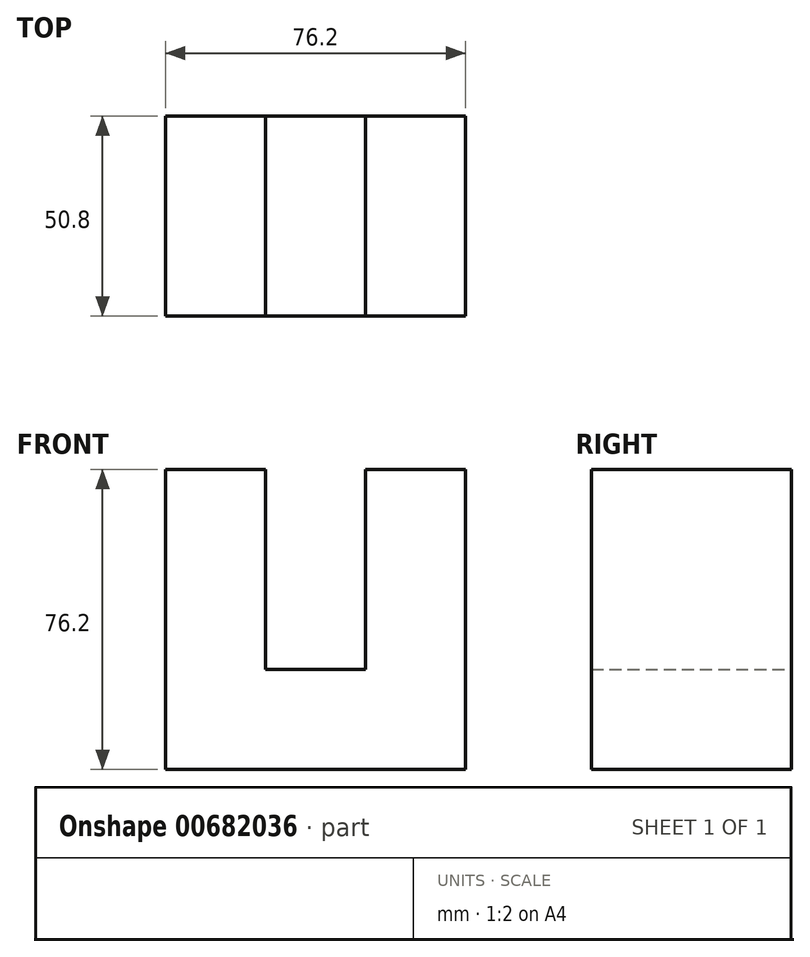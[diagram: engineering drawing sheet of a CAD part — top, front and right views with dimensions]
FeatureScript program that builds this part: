
annotation { "Feature Type Name" : "Feature", "Feature Type Description" : "" }
export const myFeature = defineFeature(function(context is Context, id is Id, definition is map)
    precondition{}
    {
        {
            var Q0;
            Q0=qCreatedBy(makeId("Front.planeOp"),FACE);
            var sketch = newSketch(context, id + "F0", { "sketchPlane" : qUnion([Q0])});
            skLineSegment(sketch, "E0", {"start": v(-52.23, 76.2) * mm, "end": v(-52.23, 0) * mm});
            skLineSegment(sketch, "E1", {"start": v(-52.23, 0) * mm, "end": v(23.97, 0) * mm});
            skLineSegment(sketch, "E2", {"start": v(23.97, 0) * mm, "end": v(23.97, 76.2) * mm});
            skLineSegment(sketch, "E3", {"start": v(-52.23, 76.2) * mm, "end": v(-26.83, 76.2) * mm});
            skLineSegment(sketch, "E4", {"start": v(23.97, 76.2) * mm, "end": v(-1.43, 76.2) * mm});
            skLineSegment(sketch, "E5", {"start": v(-26.83, 76.2) * mm, "end": v(-26.83, 25.4) * mm});
            skLineSegment(sketch, "E6", {"start": v(-1.43, 76.2) * mm, "end": v(-1.43, 25.4) * mm});
            skLineSegment(sketch, "E7", {"start": v(-26.83, 25.4) * mm, "end": v(-1.43, 25.4) * mm});
            skSolve(sketch);
        }
        {
            var Q0;
            Q0 = qSketchRegion(id + "F0", true);
            extrude(context, id + "F1", {"entities" : qUnion([Q0]), "depth" : 50.8 * mm, "offsetDistance" : 25.4 * mm});
        }
    });
